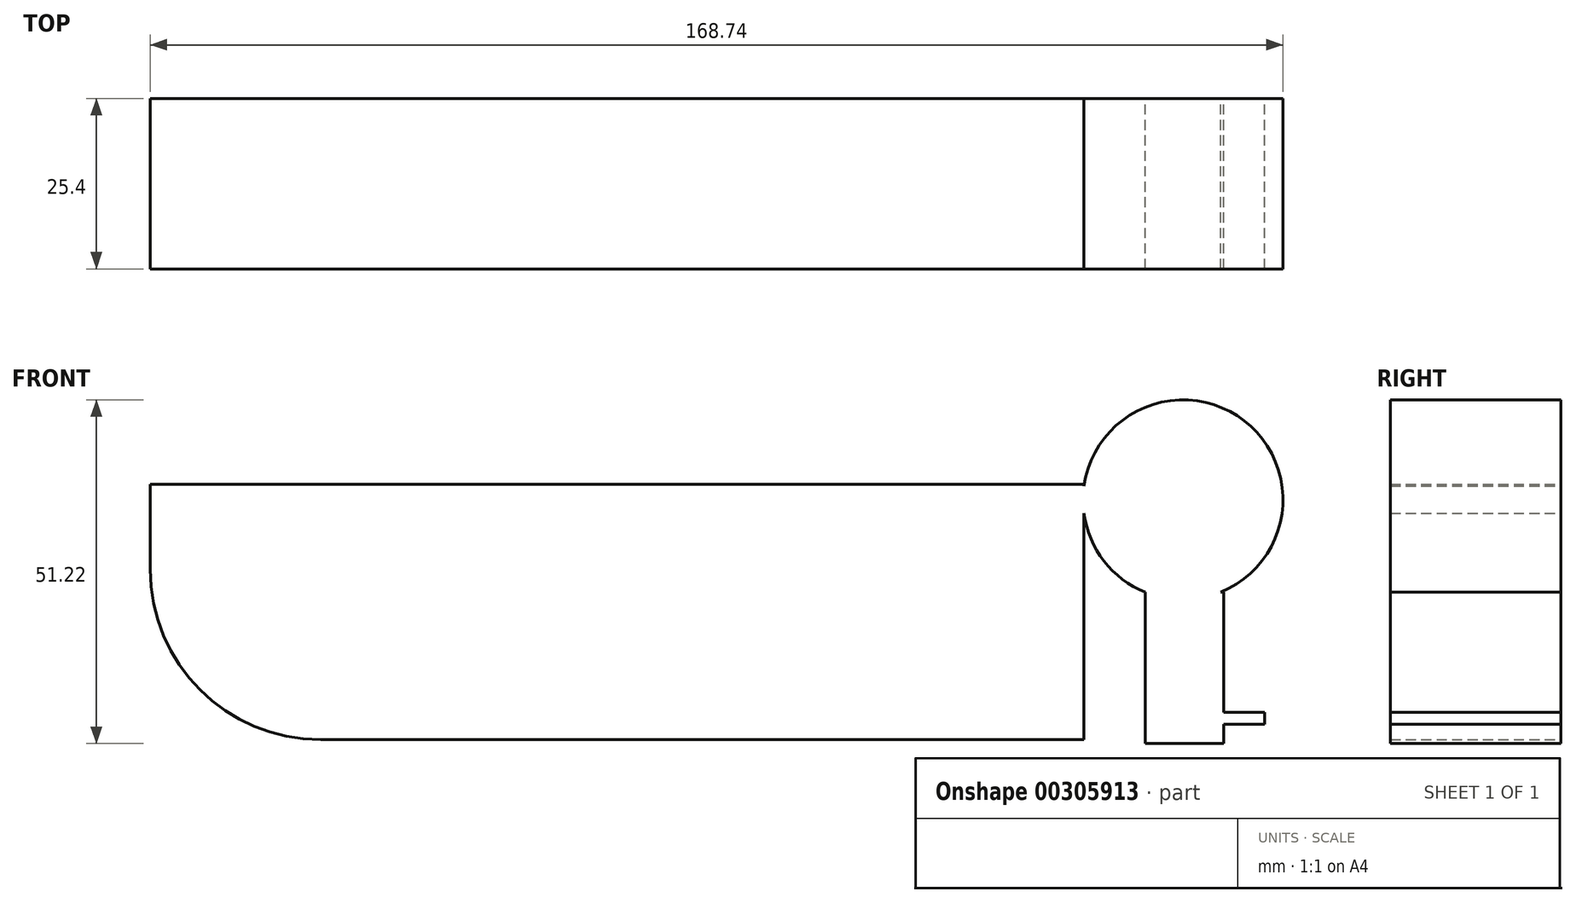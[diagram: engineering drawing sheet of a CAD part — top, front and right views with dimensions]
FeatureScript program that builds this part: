
annotation { "Feature Type Name" : "Feature", "Feature Type Description" : "" }
export const myFeature = defineFeature(function(context is Context, id is Id, definition is map)
    precondition{}
    {
        {
            var Q0;
            Q0=qCreatedBy(makeId("Front.planeOp"),FACE);
            var sketch = newSketch(context, id + "F0", { "sketchPlane" : qUnion([Q0])});
            skArc(sketch, "E0.filletArc", {"start": v(-40.37, -28.81) * mm, "mid": v(-39.17, -29.84) * mm, "end": v(-37.66, -30.27) * mm});
            skLineSegment(sketch, "E1.bottom", {"start": v(63.2, 41.1) * mm, "end": v(-75.9, 41.1) * mm});
            skLineSegment(sketch, "E1.top", {"start": v(63.2, 3.05) * mm, "end": v(-50.5, 3.05) * mm});
            skLineSegment(sketch, "E1.left", {"start": v(63.2, 41.1) * mm, "end": v(63.2, 3.05) * mm});
            skLineSegment(sketch, "E1.right", {"start": v(-75.9, 41.1) * mm, "end": v(-75.9, 28.45) * mm});
            skPoint(sketch, "E2.visualSharp", {"position": v(-75.9, 3.05) * mm});
            skArc(sketch, "E2.filletArc", {"start": v(-75.9, 28.45) * mm, "mid": v(-68.46, 10.5) * mm, "end": v(-50.5, 3.05) * mm});
            skPoint(sketch, "E3.visualSharp", {"position": v(-75.9, 28.45) * mm});
            skLineSegment(sketch, "E3.filletArc", {"start": v(-75.9, 28.45) * mm, "end": v(-75.9, 28.45) * mm});
            skPoint(sketch, "E4.visualSharp", {"position": v(-50.5, 3.05) * mm});
            skLineSegment(sketch, "E4.filletArc", {"start": v(-50.5, 3.05) * mm, "end": v(-50.5, 3.05) * mm});
            skCircle(sketch, "E5", {"center": v(77.95, 38.8) * mm, "radius": 14.89 * mm});
            skLineSegment(sketch, "E6.bottom", {"start": v(72.33, 25.01) * mm, "end": v(84.04, 25.01) * mm});
            skLineSegment(sketch, "E6.top", {"start": v(72.33, 2.47) * mm, "end": v(84.04, 2.47) * mm});
            skLineSegment(sketch, "E6.left", {"start": v(72.33, 25.01) * mm, "end": v(72.33, 2.47) * mm});
            skLineSegment(sketch, "E6.right", {"start": v(84.04, 25.01) * mm, "end": v(84.04, 2.47) * mm});
            skLineSegment(sketch, "E7.bottom", {"start": v(84.04, 7.12) * mm, "end": v(90.14, 7.12) * mm});
            skLineSegment(sketch, "E7.top", {"start": v(84.04, 5.38) * mm, "end": v(90.14, 5.38) * mm});
            skLineSegment(sketch, "E7.left", {"start": v(84.04, 7.12) * mm, "end": v(84.04, 5.38) * mm});
            skLineSegment(sketch, "E7.right", {"start": v(90.14, 7.12) * mm, "end": v(90.14, 5.38) * mm});
            skPoint(sketch, "E8.oppositeSnap0", {"position": v(87.1, 7.12) * mm});
            skLineSegment(sketch, "E8.bottom", {"start": v(87.1, 7.12) * mm, "end": v(87.1, 7.12) * mm});
            skLineSegment(sketch, "E8.top", {"start": v(87.1, 12.93) * mm, "end": v(87.1, 12.93) * mm});
            skLineSegment(sketch, "E8.left", {"start": v(87.1, 7.12) * mm, "end": v(87.1, 12.93) * mm});
            skLineSegment(sketch, "E8.right", {"start": v(87.1, 7.12) * mm, "end": v(87.1, 12.93) * mm});
            skPoint(sketch, "E9.oppositeSnap0", {"position": v(87.1, 5.38) * mm});
            skLineSegment(sketch, "E9.bottom", {"start": v(87.1, 5.38) * mm, "end": v(87.1, 5.38) * mm});
            skLineSegment(sketch, "E9.top", {"start": v(87.1, 2.47) * mm, "end": v(87.1, 2.47) * mm});
            skLineSegment(sketch, "E9.left", {"start": v(87.1, 5.38) * mm, "end": v(87.1, 2.47) * mm});
            skLineSegment(sketch, "E9.right", {"start": v(87.1, 5.38) * mm, "end": v(87.1, 2.47) * mm});
            skSolve(sketch);
        }
        {
            var Q0;
            {var subQ4=sQuery(id+"F0.wireOp",EDGE,"E1.bottom");Q0=makeQuery(id+"F0.imprint","IMPRINT",FACE,{"disambiguationData":[TD([[makeQuery(id+"F0.imprint","IMPRINT",EDGE,{"derivedFrom":subQ4}),1.0]])]});}
            var Q1;
            Q1 = qSketchRegion(id + "F0", true);
            extrude(context, id + "F1", {"entities" : qUnion([Q0, Q1]), "depth" : 25.4 * mm});
        }
    });
